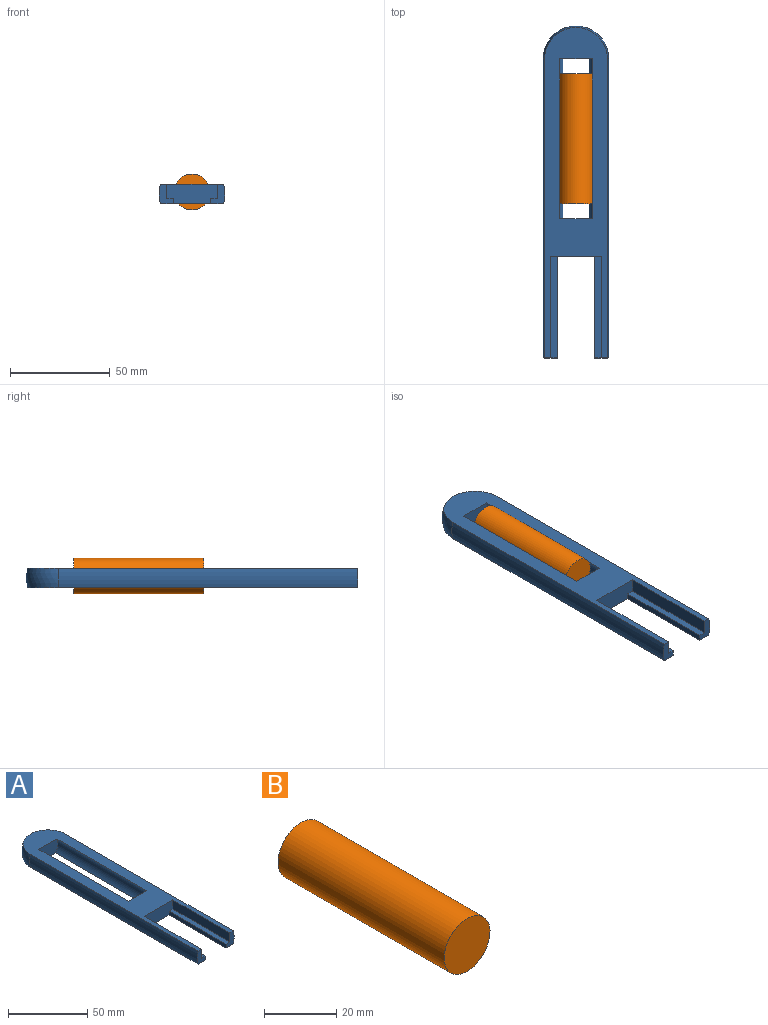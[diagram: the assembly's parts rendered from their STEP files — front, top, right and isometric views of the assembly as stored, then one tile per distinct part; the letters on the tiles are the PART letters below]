
ASSEMBLY  parts=2 mates=1
PART A: 18 faces, bbox 33x166.5x10 mm
  f0: plane 165.72x31.45mm, normal (0,0,1), area 2515.7mm2, adj f1,f2,f4,f5,f6,f9,f10,f13
  f1: plane 10x7.18mm, normal (0,-1,0), area 45.4mm2, adj f0,f2,f3,f10,f11,f12
  f2: cylinder r=16.5mm len=150mm, axis (0,1,0), area 1524mm2, adj f0,f1,f3,f6
  f3: plane 165.72x31.45mm, normal (0,0,-1), area 3079.4mm2, adj f1,f2,f4,f5,f6,f7,f12,f13
  f4: cylinder r=16.5mm len=150mm, axis (0,1,0), area 1524mm2, adj f0,f3,f5,f6
  f5: plane 10x7.18mm, normal (0,-1,0), area 45.4mm2, adj f0,f3,f4,f7,f8,f9
  f6: sphere r=16.5mm, area 518.4mm2, adj f0,f2,f3,f4
  f7: plane 51x2.96mm, normal (-1,0,0), area 151.1mm2, adj f3,f5,f8,f13
  f8: plane 51x3.4mm, normal (0,0,1), area 173.2mm2, adj f5,f7,f9,f13
  f9: plane 51x7.04mm, normal (-1,0,0), area 358.9mm2, adj f0,f5,f8,f13
  f10: plane 51x7.04mm, normal (1,0,0), area 358.9mm2, adj f0,f1,f11,f13
  f11: plane 51x3.4mm, normal (0,0,1), area 173.2mm2, adj f1,f10,f12,f13
  f12: plane 51x2.96mm, normal (1,0,0), area 151.1mm2, adj f1,f3,f11,f13
  f13: plane 25.43x10mm, normal (0,-1,0), area 234.1mm2, adj f0,f3,f7,f8,f9,f10,f11,f12
  f14: cylinder r=9mm len=80.2mm, axis (0,1,0), area 859.1mm2, adj f0,f3,f16,f17
  f15: cylinder r=9mm len=80.2mm, axis (0,1,0), area 859.1mm2, adj f0,f3,f16,f17
  f16: plane 18x10mm, normal (0,1,0), area 168.9mm2, adj f0,f3,f14,f15
  f17: plane 18x10mm, normal (0,-1,0), area 168.9mm2, adj f0,f3,f14,f15
PART B: 3 faces, bbox 18x65.2x18 mm
  f0: cylinder r=9mm len=65.2mm, axis (0,1,0), area 3687mm2, adj f1,f2
  f1: plane 18x18mm, normal (0,-1,0), area 254.5mm2, adj f0
  f2: plane 18x18mm, normal (0,1,0), area 254.5mm2, adj f0
PLACE A at identity fixed
PLACE B t=(66.93,-7.5,-44.83)mm
MATE revolute B.f0 <-> A.f14  axis (0,1,0) through (0,-40.1,1)mm
